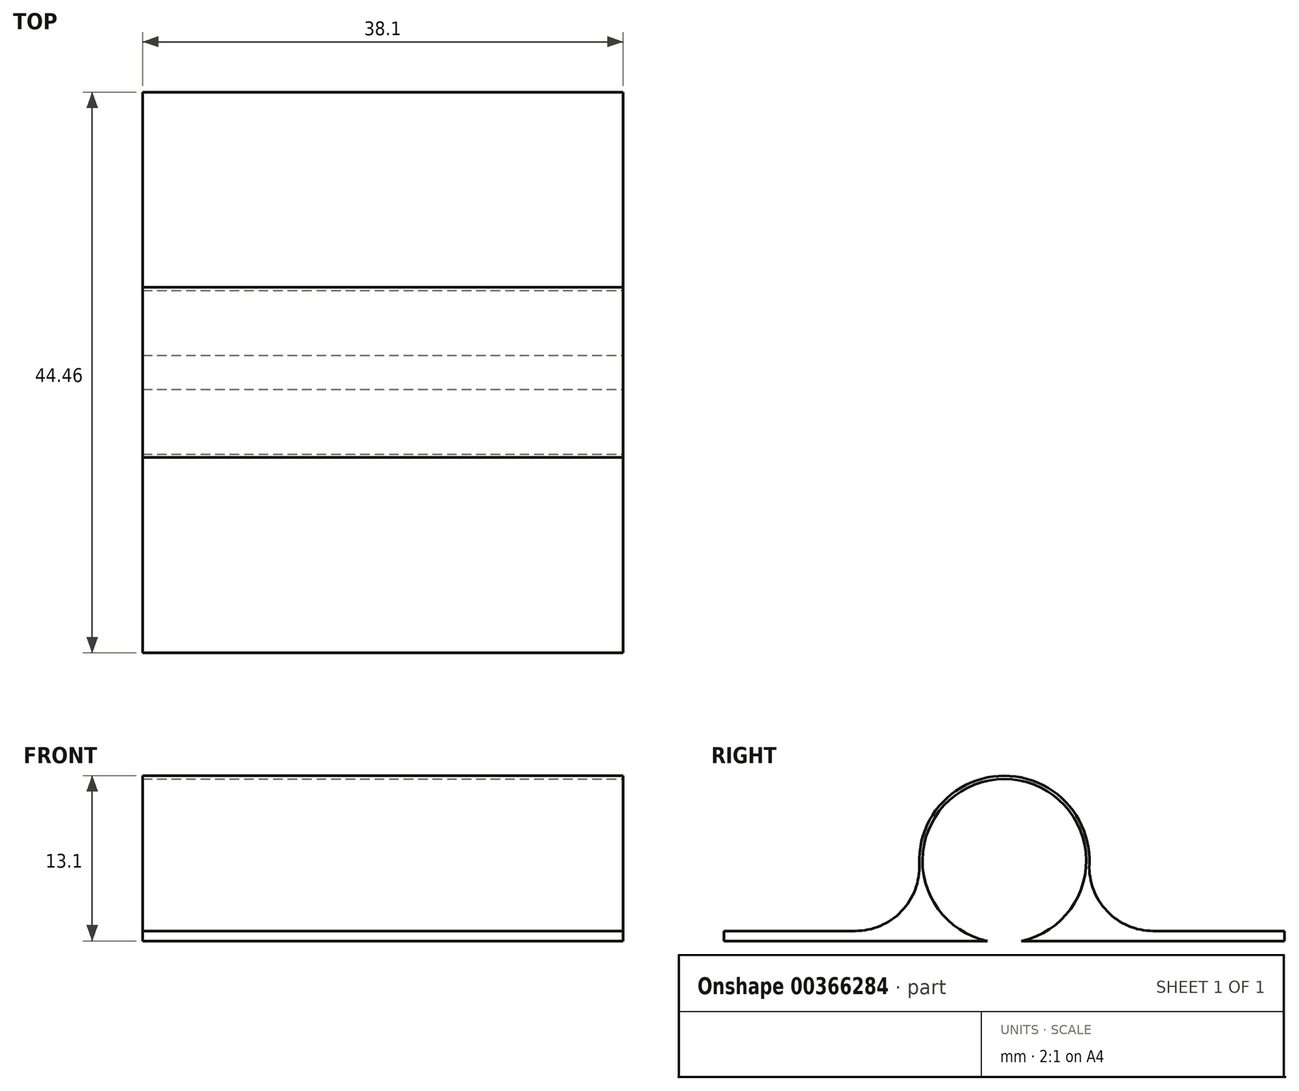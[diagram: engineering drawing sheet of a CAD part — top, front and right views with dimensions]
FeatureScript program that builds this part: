
annotation { "Feature Type Name" : "Feature", "Feature Type Description" : "" }
export const myFeature = defineFeature(function(context is Context, id is Id, definition is map)
    precondition{}
    {
        {
            var Q0;
            Q0=qCreatedBy(makeId("Right.planeOp"),FACE);
            var sketch = newSketch(context, id + "F0", { "sketchPlane" : qUnion([Q0])});
            skLineSegment(sketch, "E0", {"start": v(-22.23, 0) * mm, "end": v(-22.23, 0.8) * mm});
            skLineSegment(sketch, "E1", {"start": v(-22.23, 0.8) * mm, "end": v(-3.83, 0.8) * mm});
            skArc(sketch, "E2", {"start": v(3.83, 0.8) * mm, "mid": v(0, 13.1) * mm, "end": v(-3.83, 0.8) * mm});
            skLineSegment(sketch, "E3", {"start": v(0, 0) * mm, "end": v(-22.23, 0) * mm});
            skLineSegment(sketch, "E4.MirrorCS", {"start": v(0, 0) * mm, "end": v(22.23, 0) * mm});
            skLineSegment(sketch, "E5.MirrorCS", {"start": v(22.23, 0.8) * mm, "end": v(3.83, 0.8) * mm});
            skLineSegment(sketch, "E6.MirrorCS", {"start": v(22.23, 0) * mm, "end": v(22.23, 0.8) * mm});
            skSolve(sketch);
        }
        {
            var Q0;
            Q0=makeQuery(id+"F0.imprint","IMPRINT",FACE,{"disambiguationData":[TD([[makeQuery(id+"F0.imprint","IMPRINT",EDGE,{"derivedFrom":sQuery(id+"F0.wireOp",EDGE,"E0")}),-1.0]])]});
            extrude(context, id + "F1", {"entities" : qUnion([Q0]), "depth" : 38.1 * mm});
        }
        {
            var Q0;
            Q0=makeQuery(id+"F1.opExtrude","CAP_FACE",FACE,{"disambiguationData":[OSD([sQuery(id+"F0.wireOp",EDGE,"E0"),sQuery(id+"F0.wireOp",EDGE,"E1"),sQuery(id+"F0.wireOp",EDGE,"E2"),sQuery(id+"F0.wireOp",EDGE,"E3"),sQuery(id+"F0.wireOp",EDGE,"E4.MirrorCS"),sQuery(id+"F0.wireOp",EDGE,"E5.MirrorCS"),sQuery(id+"F0.wireOp",EDGE,"E6.MirrorCS")])],"isStart":false});
            var sketch = newSketch(context, id + "F2", { "sketchPlane" : qUnion([Q0])});
            skArc(sketch, "E7", {"start": v(1.35, 0) * mm, "mid": v(0, 12.84) * mm, "end": v(-1.35, 0) * mm});
            skLineSegment(sketch, "E8", {"start": v(-1.35, 0) * mm, "end": v(1.35, 0) * mm});
            skSolve(sketch);
        }
        {
            var Q0;
            Q0 = qSketchRegion(id + "F2", true);
            extrude(context, id + "F3", {"entities" : qUnion([Q0]), "operationType" : NewBodyOperationType.REMOVE, "endBound" : BoundingType.THROUGH_ALL, "oppositeDirection" : true, "depth" : 25.4 * mm});
        }
        {
            var Q0;
            Q0=makeQuery(id+"F1.opExtrude","SWEPT_EDGE",EDGE,{"disambiguationData":[OSD([sQuery(id+"F0.wireOp",EDGE,"E1"),sQuery(id+"F0.wireOp",EDGE,"E2")])]});
            var Q1;
            Q1=makeQuery(id+"F1.opExtrude","SWEPT_EDGE",EDGE,{"disambiguationData":[OSD([sQuery(id+"F0.wireOp",EDGE,"E2"),sQuery(id+"F0.wireOp",EDGE,"E5.MirrorCS")])]});
            fillet(context, id + "F4", {"entities" : qUnion([Q0, Q1]), "radius" : 5.08 * mm, "tangentPropagation" : true, "allowEdgeOverflow" : false});
        }
        {
            var Q0;
            {var subQ0=sQuery(id+"F2.wireOp",EDGE,"E7");Q0=makeQuery(id+"F2.imprint","IMPRINT",FACE,{"disambiguationData":[TD([[makeQuery(id+"F2.imprint","IMPRINT",EDGE,{"derivedFrom":subQ0}),1.0]])]});}
            extrude(context, id + "F5", {"entities" : qUnion([Q0]), "operationType" : NewBodyOperationType.REMOVE, "endBound" : BoundingType.THROUGH_ALL, "oppositeDirection" : true, "depth" : 25.4 * mm});
        }
    });
